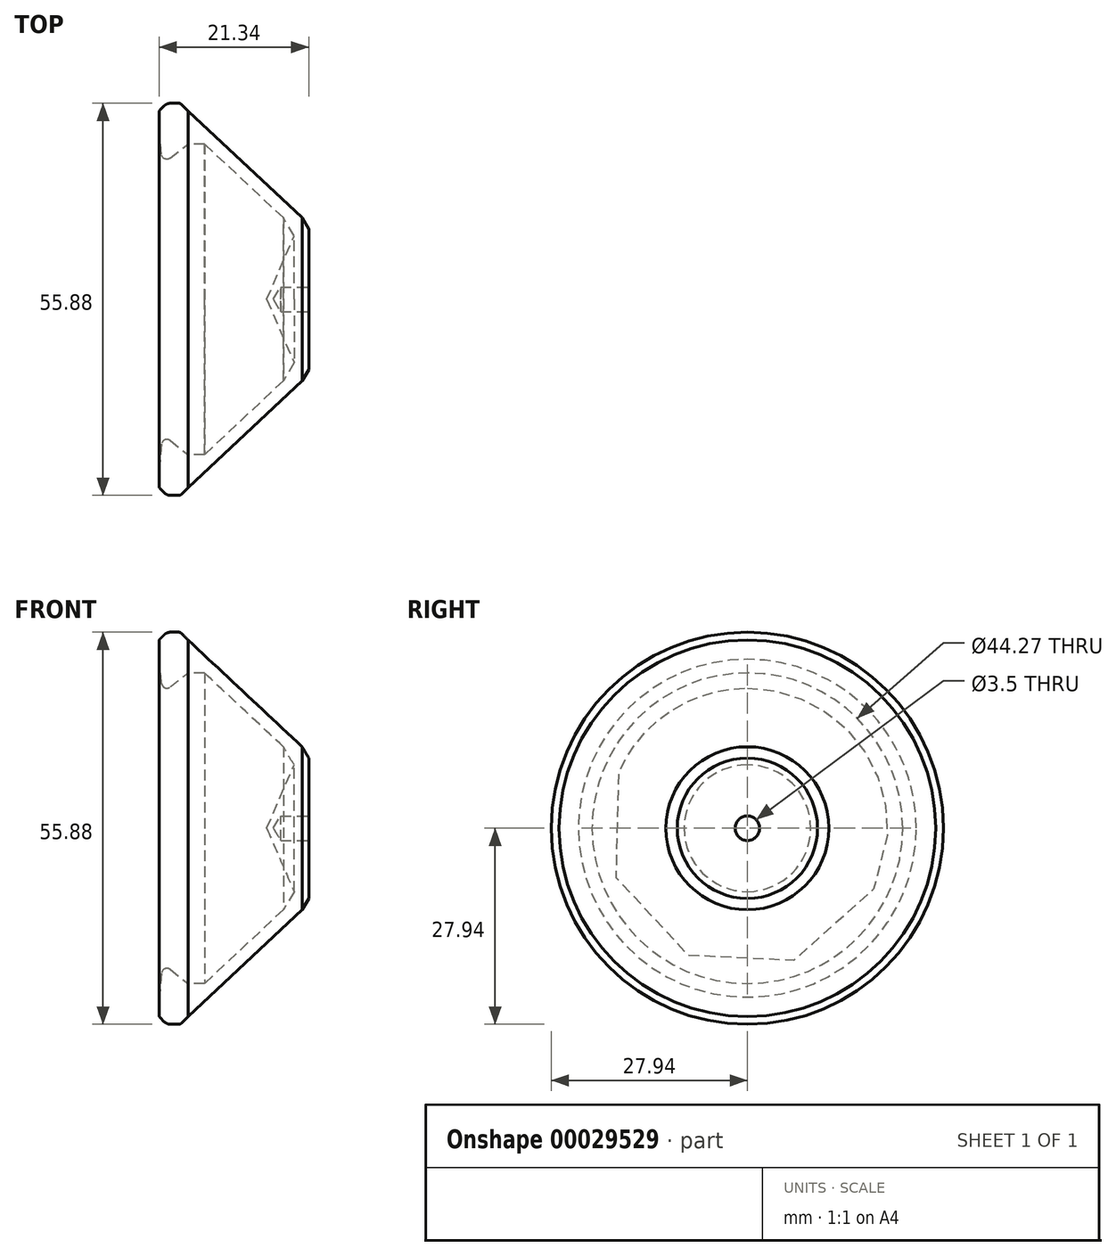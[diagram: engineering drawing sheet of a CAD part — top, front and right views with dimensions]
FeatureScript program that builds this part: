
annotation { "Feature Type Name" : "Feature", "Feature Type Description" : "" }
export const myFeature = defineFeature(function(context is Context, id is Id, definition is map)
    precondition{}
    {
        {
            var Q0;
            Q0=qCreatedBy(makeId("Front.planeOp"),FACE);
            var sketch = newSketch(context, id + "F0", { "sketchPlane" : qUnion([Q0])});
            skLineSegment(sketch, "E0", {"start": v(0, 0) * mm, "end": v(21.34, 0) * mm, "construction": true});
            skLineSegment(sketch, "E1", {"start": v(0, 0) * mm, "end": v(0, 27.94) * mm, "construction": true});
            skLineSegment(sketch, "E2", {"start": v(21.34, 0) * mm, "end": v(21.34, 10) * mm});
            skLineSegment(sketch, "E3", {"start": v(4.13, 26.83) * mm, "end": v(3.17, 27.8) * mm});
            skLineSegment(sketch, "E4", {"start": v(2.8, 27.94) * mm, "end": v(1.63, 27.94) * mm});
            skLineSegment(sketch, "E5", {"start": v(0.74, 27.57) * mm, "end": v(0.15, 26.98) * mm});
            skLineSegment(sketch, "E6", {"start": v(21.34, 10) * mm, "end": v(20.39, 11.61) * mm});
            skLineSegment(sketch, "E7", {"start": v(20.39, 11.61) * mm, "end": v(4.13, 26.83) * mm});
            skLineSegment(sketch, "E8", {"start": v(0, 26.62) * mm, "end": v(0, 24.07) * mm});
            skLineSegment(sketch, "E9", {"start": v(0, 24.07) * mm, "end": v(0.36, 20.65) * mm});
            skLineSegment(sketch, "E10", {"start": v(1.59, 20.13) * mm, "end": v(4.13, 22.14) * mm});
            skLineSegment(sketch, "E11", {"start": v(4.13, 22.14) * mm, "end": v(6.48, 22.14) * mm});
            skLineSegment(sketch, "E12", {"start": v(6.48, 22.14) * mm, "end": v(17.72, 11.61) * mm});
            skLineSegment(sketch, "E13", {"start": v(17.72, 11.61) * mm, "end": v(19.24, 9.03) * mm});
            skLineSegment(sketch, "E14", {"start": v(19.24, 9.03) * mm, "end": v(15.34, 0) * mm});
            skLineSegment(sketch, "E15", {"start": v(15.34, 0) * mm, "end": v(21.34, 0) * mm});
            skPoint(sketch, "E16.visualSharp", {"position": v(1.1, 27.94) * mm});
            skArc(sketch, "E16.filletArc", {"start": v(1.63, 27.94) * mm, "mid": v(1.15, 27.84) * mm, "end": v(0.74, 27.57) * mm});
            skPoint(sketch, "E17.visualSharp", {"position": v(3.02, 27.94) * mm});
            skArc(sketch, "E17.filletArc", {"start": v(3.17, 27.8) * mm, "mid": v(3, 27.9) * mm, "end": v(2.8, 27.94) * mm});
            skPoint(sketch, "E18.visualSharp", {"position": v(0, 26.83) * mm});
            skArc(sketch, "E18.filletArc", {"start": v(0.15, 26.98) * mm, "mid": v(0.04, 26.82) * mm, "end": v(0, 26.62) * mm});
            skPoint(sketch, "E19.visualSharp", {"position": v(0.5, 19.27) * mm});
            skArc(sketch, "E19.filletArc", {"start": v(0.36, 20.65) * mm, "mid": v(0.82, 20.03) * mm, "end": v(1.59, 20.13) * mm});
            skSolve(sketch);
        }
        {
            var Q0;
            Q0=makeQuery(id+"F0.imprint","IMPRINT",FACE,{"disambiguationData":[TD([[makeQuery(id+"F0.imprint","IMPRINT",EDGE,{"derivedFrom":sQuery(id+"F0.wireOp",EDGE,"E2")}),1.0]])]});
            var Q1;
            Q1=sQuery(id+"F0.wireOp",EDGE,"E15");
            revolve(context, id + "F1", {"entities" : qUnion([Q0]), "axis" : qUnion([Q1]), "revolveType" : RevolveType.FULL});
        }
        {
            var Q0;
            Q0=makeQuery(id+"F1.opRevolve","SWEPT_FACE",FACE,{"disambiguationData":[OSD([sQuery(id+"F0.wireOp",EDGE,"E2")])]});
            var sketch = newSketch(context, id + "F2", { "sketchPlane" : qUnion([Q0])});
            skPoint(sketch, "E20", {"position": v(0, 0) * mm});
            skSolve(sketch);
        }
        {
            var Q0;
            Q0=sQuery(id+"F2.wireOp",VERTEX,"E20");
            var Q1;
            Q1=makeQuery(id+"F1.opRevolve","SWEPT_BODY",BODY,{"disambiguationData":[OSD([sQuery(id+"F0.wireOp",EDGE,"E2"),sQuery(id+"F0.wireOp",EDGE,"E3"),sQuery(id+"F0.wireOp",EDGE,"E4"),sQuery(id+"F0.wireOp",EDGE,"E5"),sQuery(id+"F0.wireOp",EDGE,"E6"),sQuery(id+"F0.wireOp",EDGE,"E7"),sQuery(id+"F0.wireOp",EDGE,"E8"),sQuery(id+"F0.wireOp",EDGE,"E9"),sQuery(id+"F0.wireOp",EDGE,"E10"),sQuery(id+"F0.wireOp",EDGE,"E11"),sQuery(id+"F0.wireOp",EDGE,"E12"),sQuery(id+"F0.wireOp",EDGE,"E13"),sQuery(id+"F0.wireOp",EDGE,"E14"),sQuery(id+"F0.wireOp",EDGE,"E15"),sQuery(id+"F0.wireOp",EDGE,"E16.filletArc"),sQuery(id+"F0.wireOp",EDGE,"E17.filletArc"),sQuery(id+"F0.wireOp",EDGE,"E18.filletArc"),sQuery(id+"F0.wireOp",EDGE,"E19.filletArc")])]});
            hole(context, id + "F3", {"style" : HoleStyle.SIMPLE, "holeDiameter" : 3.5 * mm, "endStyle" : HoleEndStyle.BLIND, "holeDepth" : 4 * mm, "locations" : qUnion([Q0]), "scope" : qUnion([Q1])});
        }
    });
